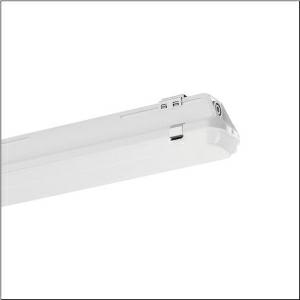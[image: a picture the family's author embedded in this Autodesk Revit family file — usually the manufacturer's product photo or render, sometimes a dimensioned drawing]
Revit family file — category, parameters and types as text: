
# Revit family: monsun_21_emergency_51fb207p437c3g
name_source: partatom
category: Lighting Fixtures
units: mm (PartAtom-declared; Revit-internal decimal feet)

## family parameters
Cut with Voids When Loaded = No
Host = Face
Light Source = No
Part Type = Normal
Room Calculation Point = No
Round Connector Dimension = Use Diameter
Shared = No

## types (1)
- --- (1 x LED, 820 lm, 7.1 W, 4000K)
    Apparent Load = 7 VA
    CIE Flux Codes = 45 75 93 94 100
    Color Rendering = 80
    Color Temperature = 4000K
    Default Elevation = 1800 mm
    Description = Monsun 21 emergency, damp-proof luminaire, chain hanger, primary optical cover: enclosure, of PC, light emission: direct distribution, primary light characteristic: symmetric, installation type: suspended mounting, surface-mounted, horizontal mounting, vertical mounting, LED, rated luminous flux: 3.620lm, luminous efficacy: 157lm/W, light colour: 840, colour temperature: 4000K, control gear: ON/OFF, with terminal, 4-pole, max. 2.5mm², mains connection: 220..240V, AC, 50/60Hz, rated input power: 27W, control gear: single battery element, battery: LiFePO4, 9Ah, housing, of glass-fibre reinforced polyester, uncoated, bright grey, incl. chain hanger, length: 1.590mm, width: 90mm, height: 88mm, clip for enclosure, of stainless steel (V2A), ceiling mounting element, of stainless steel (V2A), chain hanger, of stainless steel (V2A), protection rating (complete): IP66, insulation class (complete): insulation class I (protective earthing), certification: CE, UKCA, protection symbol: D, impact resistance: IK08, permissible operating ambient temperature: +5..+25°C, standard: EN 50419, EN 60598-2-1, EN 60598-2-22, corresponds to IFS (International Featured Standards) requirements for safety and quality in the food industry, for indoor or canopied outdoor use, no direct snow, no direct sun, no direct rain, LABS conformity tested according to VDMA 24364:2018-05, contact your sales advisor before using the luminaires in applications with unclear chemical exposure, large temperature fluctuations or condensation-forming humidity, packaging unit: 1 piece
    Height = 89 mm
    Lamp = 1 x LED
    Lamp Light Flux = 820 lm
    Lamp Power = 7.1 W
    Lamp count = 1
    Length = 1590 mm
    Luminous efficacy = 115 lm/W
    Manufacturer = Siteco
    ModVariant = No
    Model = 51FB207P437C3G
    Mounting Place = Ceiling
    Mounting Type = Surface mounted
    Number of Poles = 1
    OnlyDefault = Yes
    Power Factor = 1
    Product Name = Monsun 21 emergency
    Product group = damp-proof luminaire
    ProductGroupID = 300
    Protection Class = Protection class I
    Protection Degree = IP 66
    RLX_Detail_Level = 1
    RLX_Emergency_Light_Flux = 0 lm
    RLX_Emergency_Type = 0
    RLX_Emergency_Type_DB = No
    RlxData = <blob elided: 88753 chars, md5=05d72e04>
    Socket = socket
    Standby Power = 0 W
    System Light Flux = 820 lm
    System Power = 7 W
    Type Comments = : emergency light operation: 3 h
    Type Image = l_1319656.jpg
    URL = http://relux.com
    VarID = @adj_049317
    Voltage = 0 V
    Weight = 0.00 kg
    Width = 90 mm

## geometry (parser evidence)
native form markers: Blend x4, Sweep x13
no freeform markers — native parametric forms only
